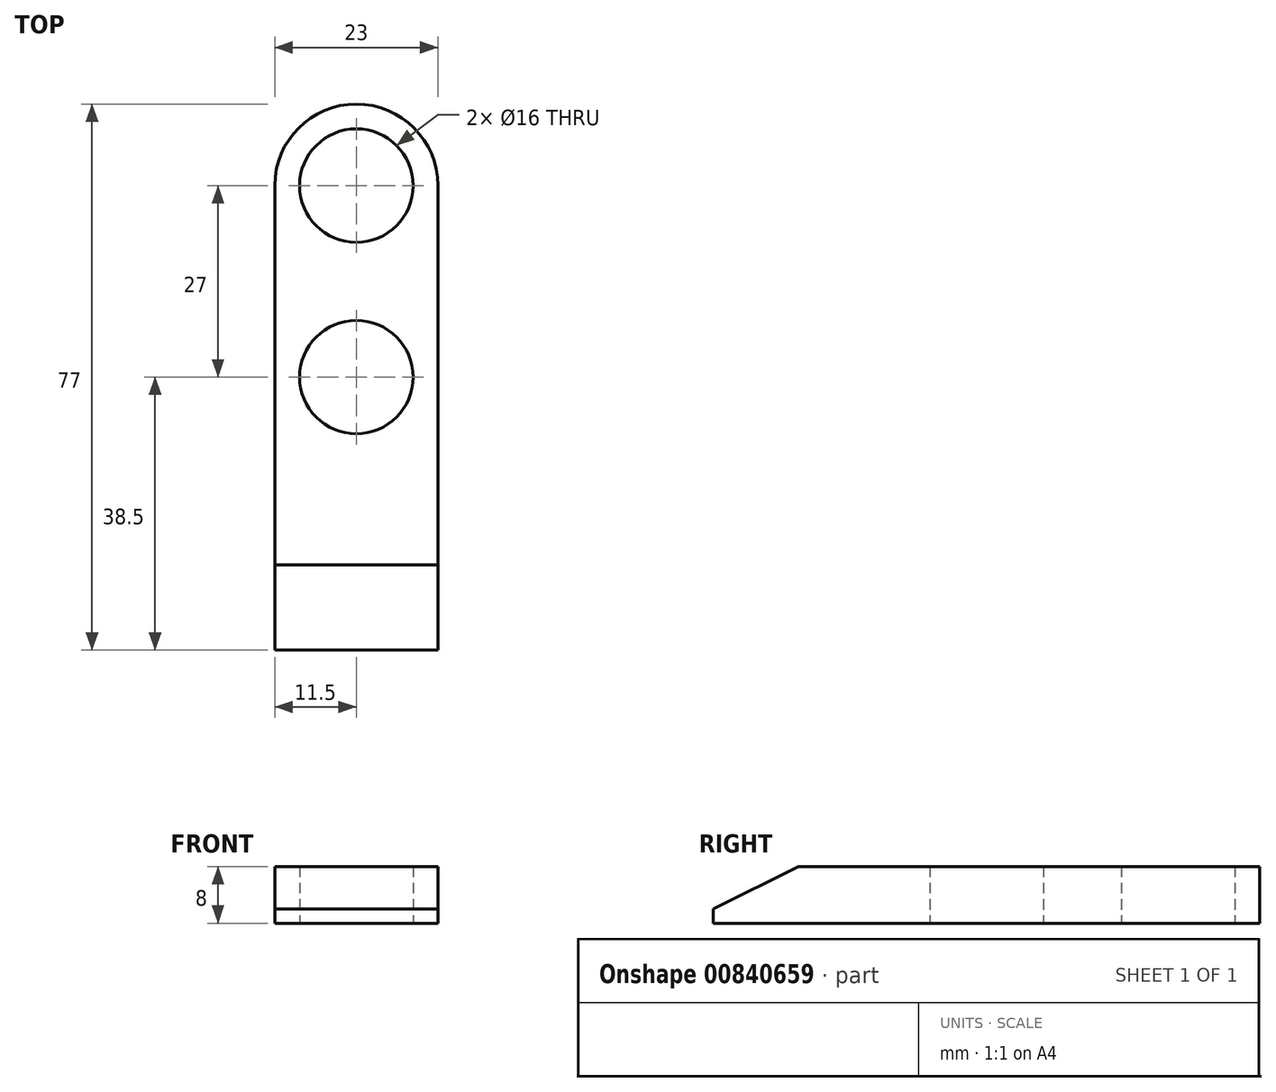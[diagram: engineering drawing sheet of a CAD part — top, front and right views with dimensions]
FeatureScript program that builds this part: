
annotation { "Feature Type Name" : "Feature", "Feature Type Description" : "" }
export const myFeature = defineFeature(function(context is Context, id is Id, definition is map)
    precondition{}
    {
        {
            var Q0;
            Q0=qCreatedBy(makeId("Top.planeOp"),FACE);
            var sketch = newSketch(context, id + "F0", { "sketchPlane" : qUnion([Q0])});
            skLineSegment(sketch, "E0.top", {"start": v(-11.5, -38.5) * mm, "end": v(11.5, -38.5) * mm});
            skLineSegment(sketch, "E0.left", {"start": v(-11.5, 27) * mm, "end": v(-11.5, -38.5) * mm});
            skLineSegment(sketch, "E0.right", {"start": v(11.5, 27) * mm, "end": v(11.5, -38.5) * mm});
            skPoint(sketch, "E0.middle", {"position": v(0, 0) * mm});
            skArc(sketch, "E1", {"start": v(11.5, 27) * mm, "mid": v(0, 38.5) * mm, "end": v(-11.5, 27) * mm});
            skCircle(sketch, "E2", {"center": v(0, 27) * mm, "radius": 8 * mm});
            skCircle(sketch, "E3", {"center": v(0, 0) * mm, "radius": 8 * mm});
            skSolve(sketch);
        }
        {
            var Q0;
            Q0=makeQuery(id+"F0.imprint","IMPRINT",FACE,{"disambiguationData":[TD([[makeQuery(id+"F0.imprint","IMPRINT",EDGE,{"derivedFrom":sQuery(id+"F0.wireOp",EDGE,"E0.top")}),1.0]])]});
            extrude(context, id + "F1", {"entities" : qUnion([Q0]), "depth" : 8 * mm, "offsetDistance" : 25 * mm});
        }
        {
            var Q0;
            Q0=makeQuery(id+"F1.opExtrude","SWEPT_FACE",FACE,{"disambiguationData":[OSD([sQuery(id+"F0.wireOp",EDGE,"E0.left")])]});
            var sketch = newSketch(context, id + "F2", { "sketchPlane" : qUnion([Q0])});
            skLineSegment(sketch, "E4", {"start": v(38.5, 2) * mm, "end": v(26.5, 8) * mm});
            skSolve(sketch);
        }
        {
            var Q0;
            {var subQ0=sQuery(id+"F2.wireOp",EDGE,"E4");Q0=makeQuery(id+"F2.imprint","IMPRINT",FACE,{"disambiguationData":[TD([[makeQuery(id+"F2.imprint","IMPRINT",EDGE,{"derivedFrom":subQ0}),-1.0]])]});}
            extrude(context, id + "F3", {"entities" : qUnion([Q0]), "operationType" : NewBodyOperationType.REMOVE, "endBound" : BoundingType.THROUGH_ALL, "oppositeDirection" : true, "depth" : 25 * mm, "offsetDistance" : 25 * mm});
        }
    });
